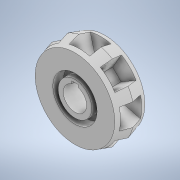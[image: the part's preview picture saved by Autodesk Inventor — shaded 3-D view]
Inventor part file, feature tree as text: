
AUTODESK INVENTOR PART (.ipt)
format: ipt  version: 2020.2 (Build 242310000, 310)  size: 200,704 bytes
history: native  units: mm
features: sketch x6, extrude x4, mirror x1, revolve x1, pattern_circular x1
ambient origin geometry x8: Origin, YZ Plane, XZ Plane, XY Plane, X Axis, Y Axis, Z Axis, Center Point
bodies: Solid1 (feature_tree)
feature tree (13):
  extrude  "Extrusion1"  Depth=17.0mm TaperAngle=0.0deg
  extrude  "Extrusion2"  Depth=3.5mm
  extrude  "Extrusion3"  TaperAngle=0.0deg  [1 undecoded]
  mirror  "Mirror1"
  revolve  "Revolution1"  [1 undecoded]
  extrude  "Extrusion4"  Depth=2.5mm
  pattern_circular  "Circular Pattern1"  [2 undecoded]
  sketch  "Sketch6"  dims[d13=90.0deg d14=13.0mm d15=12.0mm d16=12.0mm d17=0.0mm d18=80.0mm d19=360.0deg d21=41.0mm]
  sketch  "Sketch1"  dims[d0=45.0mm d1=17.0mm d2=0.0mm]
  sketch  "Sketch2"  dims[d3=13.2mm d4=3.5mm]
  sketch  "Sketch3"  dims[d5=1.5mm d6=0.0mm d7=0.0mm]
  sketch  "Sketch4"  dims[d8=19.0mm d9=3.0mm]
  sketch  "Sketch5"  dims[d10=6.0mm d11=0.0mm d12=2.5mm]
note: 4 required parameter values undecoded (feature->parameter linkage not recoverable at this tier; creation-order binding heuristic only, values carry confidence <= 0.55)